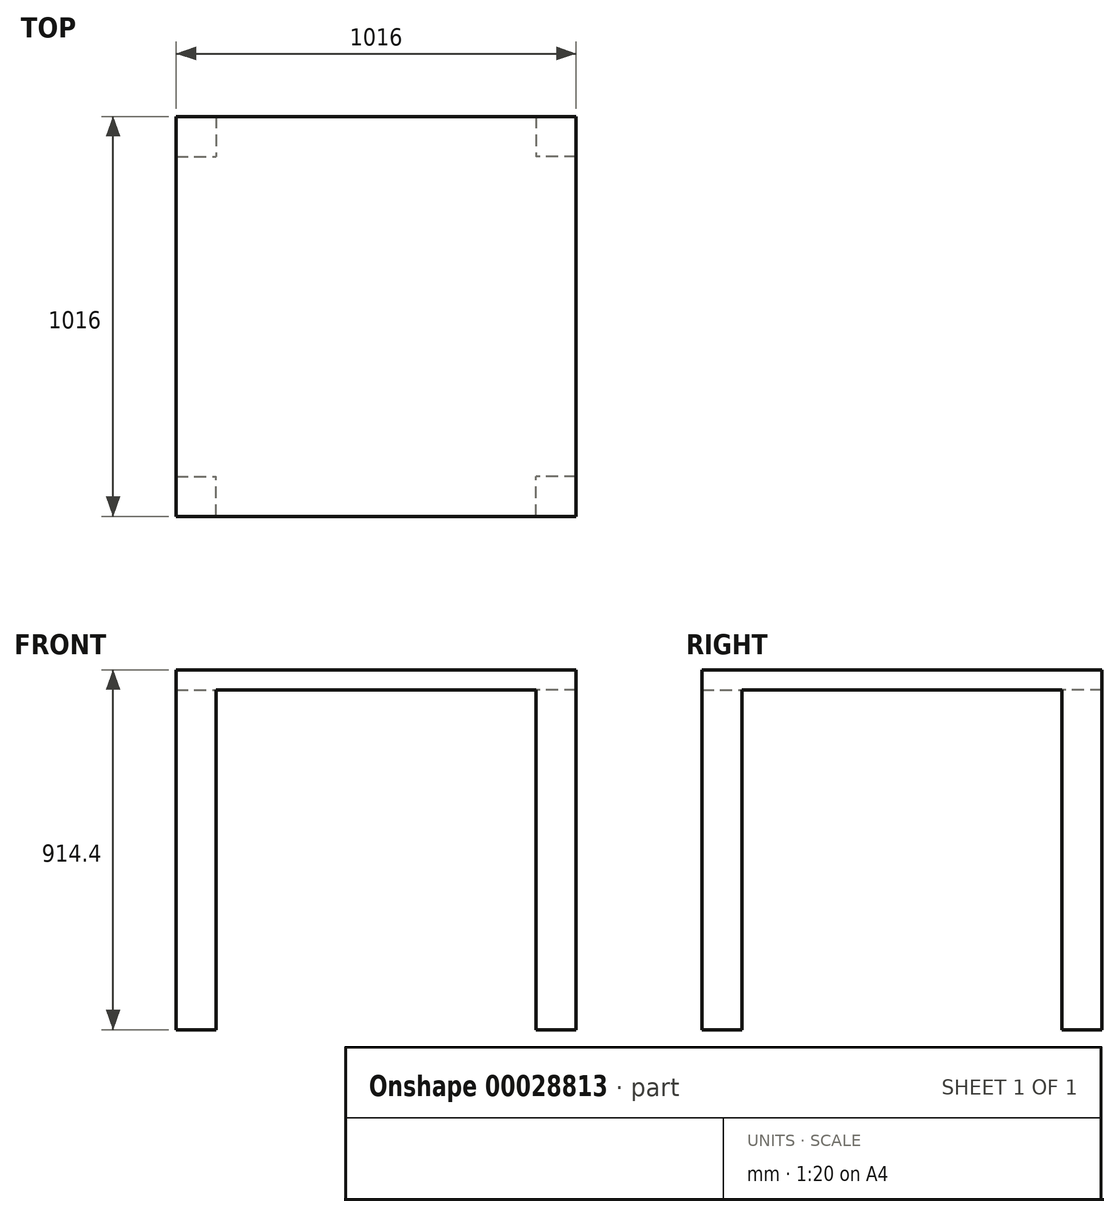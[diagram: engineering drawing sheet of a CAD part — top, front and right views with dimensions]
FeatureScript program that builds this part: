
annotation { "Feature Type Name" : "Feature", "Feature Type Description" : "" }
export const myFeature = defineFeature(function(context is Context, id is Id, definition is map)
    precondition{}
    {
        {
            var Q0;
            Q0=qCreatedBy(makeId("Top.planeOp"),FACE);
            var sketch = newSketch(context, id + "F0", { "sketchPlane" : qUnion([Q0])});
            skLineSegment(sketch, "E0.bottom", {"start": v(-603.36, 539.77) * mm, "end": v(412.64, 539.77) * mm});
            skLineSegment(sketch, "E0.top", {"start": v(-603.36, -476.23) * mm, "end": v(412.64, -476.23) * mm});
            skLineSegment(sketch, "E0.left", {"start": v(-603.36, 539.77) * mm, "end": v(-603.36, -476.23) * mm});
            skLineSegment(sketch, "E0.right", {"start": v(412.64, 539.77) * mm, "end": v(412.64, -476.23) * mm});
            skSolve(sketch);
        }
        {
            var Q0;
            Q0 = qSketchRegion(id + "F0", true);
            extrude(context, id + "F1", {"entities" : qUnion([Q0]), "depth" : 50.8 * mm});
        }
        {
            var Q0;
            Q0=makeQuery(id+"F1.opExtrude","CAP_FACE",FACE,{"disambiguationData":[OSD([sQuery(id+"F0.wireOp",EDGE,"E0.bottom"),sQuery(id+"F0.wireOp",EDGE,"E0.top"),sQuery(id+"F0.wireOp",EDGE,"E0.left"),sQuery(id+"F0.wireOp",EDGE,"E0.right")])],"isStart":true});
            var sketch = newSketch(context, id + "F2", { "sketchPlane" : qUnion([Q0])});
            skLineSegment(sketch, "E1.bottom", {"start": v(-603.36, 476.23) * mm, "end": v(-501.76, 476.23) * mm});
            skLineSegment(sketch, "E1.top", {"start": v(-603.36, 374.63) * mm, "end": v(-501.76, 374.63) * mm});
            skLineSegment(sketch, "E1.left", {"start": v(-603.36, 476.23) * mm, "end": v(-603.36, 374.63) * mm});
            skLineSegment(sketch, "E1.right", {"start": v(-501.76, 476.23) * mm, "end": v(-501.76, 374.63) * mm});
            skLineSegment(sketch, "E2.MirrorCS", {"start": v(311.04, 476.23) * mm, "end": v(311.04, 374.63) * mm});
            skLineSegment(sketch, "E3.MirrorCS", {"start": v(412.64, 374.63) * mm, "end": v(311.04, 374.63) * mm});
            skLineSegment(sketch, "E4.MirrorCS", {"start": v(412.64, 476.23) * mm, "end": v(412.64, 374.63) * mm});
            skLineSegment(sketch, "E5.MirrorCS", {"start": v(412.64, 476.23) * mm, "end": v(311.04, 476.23) * mm});
            skPoint(sketch, "E6.orphan", {"position": v(-567.01, 0) * mm});
            skLineSegment(sketch, "E7.MirrorCS", {"start": v(-501.76, -539.77) * mm, "end": v(-501.76, -438.17) * mm});
            skLineSegment(sketch, "E8.MirrorCS", {"start": v(-603.36, -438.17) * mm, "end": v(-501.76, -438.17) * mm});
            skLineSegment(sketch, "E9.MirrorCS", {"start": v(-603.36, -539.77) * mm, "end": v(-603.36, -438.17) * mm});
            skLineSegment(sketch, "E10.MirrorCS", {"start": v(-603.36, -539.77) * mm, "end": v(-501.76, -539.77) * mm});
            skLineSegment(sketch, "E11.MirrorCS", {"start": v(412.64, -539.77) * mm, "end": v(311.04, -539.77) * mm});
            skLineSegment(sketch, "E12.MirrorCS", {"start": v(311.04, -539.77) * mm, "end": v(311.04, -438.17) * mm});
            skLineSegment(sketch, "E13.MirrorCS", {"start": v(412.64, -438.17) * mm, "end": v(311.04, -438.17) * mm});
            skLineSegment(sketch, "E14.MirrorCS", {"start": v(412.64, -539.77) * mm, "end": v(412.64, -438.17) * mm});
            skPoint(sketch, "E15.orphan", {"position": v(-95.36, 476.23) * mm});
            skPoint(sketch, "E16.end.orphan", {"position": v(-95.36, -539.77) * mm});
            skPoint(sketch, "E16.start.orphan", {"position": v(-95.36, -31.77) * mm});
            skSolve(sketch);
        }
        {
            var Q0;
            Q0 = qSketchRegion(id + "F2", true);
            extrude(context, id + "F3", {"entities" : qUnion([Q0]), "operationType" : NewBodyOperationType.ADD, "depth" : 863.6 * mm});
        }
    });
